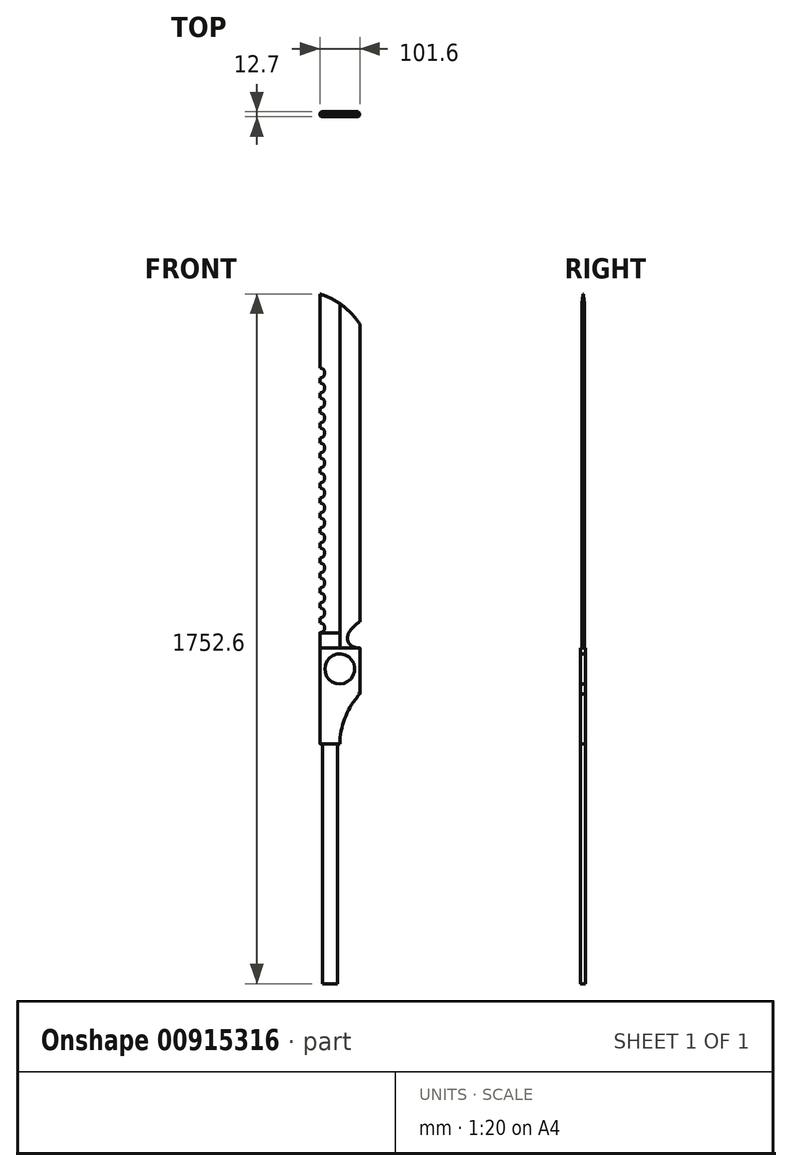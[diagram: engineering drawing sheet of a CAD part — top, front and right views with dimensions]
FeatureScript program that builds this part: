
annotation { "Feature Type Name" : "Feature", "Feature Type Description" : "" }
export const myFeature = defineFeature(function(context is Context, id is Id, definition is map)
    precondition{}
    {
        {
            var Q0;
            Q0=qCreatedBy(makeId("Front.planeOp"),FACE);
            var sketch = newSketch(context, id + "F0", { "sketchPlane" : qUnion([Q0])});
            skLineSegment(sketch, "E0", {"start": v(0, 0) * mm, "end": v(0, 381) * mm, "construction": true});
            skLineSegment(sketch, "E1", {"start": v(0, 0) * mm, "end": v(0, -609.6) * mm, "construction": true});
            skLineSegment(sketch, "E2.top", {"start": v(50.8, -762) * mm, "end": v(-50.8, -762) * mm});
            skLineSegment(sketch, "E2.left", {"start": v(50.8, 381) * mm, "end": v(50.8, -762) * mm});
            skLineSegment(sketch, "E2.right", {"start": v(-50.8, 381) * mm, "end": v(-50.8, -762) * mm});
            skPoint(sketch, "E2.middle", {"position": v(0, 0) * mm});
            skLineSegment(sketch, "E3", {"start": v(-50.8, 381) * mm, "end": v(50.8, 381) * mm});
            skLineSegment(sketch, "E4", {"start": v(25.4, 381) * mm, "end": v(25.4, 685.8) * mm, "construction": true});
            skPoint(sketch, "E5.orphan", {"position": v(0, 381) * mm});
            skPoint(sketch, "E6.orphan", {"position": v(-50.8, 762) * mm});
            skPoint(sketch, "E7.orphan", {"position": v(50.8, 762) * mm});
            skPoint(sketch, "E8.orphan", {"position": v(0, 762) * mm});
            skCircle(sketch, "E9", {"center": v(0, 190.5) * mm, "radius": 38.1 * mm});
            skPoint(sketch, "E10.orphan", {"position": v(0, 152.4) * mm});
            skLineSegment(sketch, "E11", {"start": v(0, 152.4) * mm, "end": v(0, 137.16) * mm, "construction": true});
            skLineSegment(sketch, "E12", {"start": v(-50.8, 137.16) * mm, "end": v(50.8, 137.16) * mm});
            skSolve(sketch);
        }
        {
            var Q0;
            {var subQ0=sQuery(id+"F0.wireOp",EDGE,"E3");Q0=makeQuery(id+"F0.imprint","IMPRINT",FACE,{"disambiguationData":[TD([[makeQuery(id+"F0.imprint","IMPRINT",EDGE,{"derivedFrom":subQ0}),-1.0]])]});}
            extrude(context, id + "F1", {"entities" : qUnion([Q0]), "endBound" : BoundingType.SYMMETRIC, "depth" : 12.7 * mm, "offsetDistance" : 30.48 * mm});
        }
        {
            var Q0;
            {var subQ0=sQuery(id+"F0.wireOp",EDGE,"E2.top");Q0=makeQuery(id+"F0.imprint","IMPRINT",FACE,{"disambiguationData":[TD([[makeQuery(id+"F0.imprint","IMPRINT",EDGE,{"derivedFrom":subQ0}),-1.0]])]});}
            extrude(context, id + "F2", {"entities" : qUnion([Q0]), "operationType" : NewBodyOperationType.ADD, "endBound" : BoundingType.SYMMETRIC, "depth" : 6.35 * mm, "offsetDistance" : 25.4 * mm});
        }
        {
            var Q0;
            Q0=makeQuery(id+"F1.opExtrude","SWEPT_FACE",FACE,{"disambiguationData":[OSD([sQuery(id+"F0.wireOp",EDGE,"E3")])]});
            var sketch = newSketch(context, id + "F3", { "sketchPlane" : qUnion([Q0])});
            skPoint(sketch, "E13.0", {"position": v(25.4, 0) * mm});
            skEllipse(sketch, "E14", {"center": v(25.4, 0) * mm, "majorRadius": 19.05 * mm, "minorRadius": 6.35 * mm, "majorAxis": v(-1, 0)});
            skSolve(sketch);
        }
        {
            var Q0;
            Q0 = qSketchRegion(id + "F3", true);
            extrude(context, id + "F4", {"entities" : qUnion([Q0]), "depth" : 609.6 * mm, "offsetDistance" : 30.48 * mm});
        }
        {
            var Q0;
            Q0=sQuery(id+"F0.wireOp",EDGE,"E12");
            cPlane(context, id + "F5", {"entities" : qUnion([Q0]), "cplaneType" : CPlaneType.LINE_ANGLE, "offset" : 25.4 * mm, "angle" : 90 * degree, "width" : 152.4 * mm, "height" : 152.4 * mm});
        }
        {
            var Q0;
            Q0=qCreatedBy(id+"F5.planeOp",FACE);
            var sketch = newSketch(context, id + "F6", { "sketchPlane" : qUnion([Q0])});
            skPoint(sketch, "E15.0", {"position": v(0, 0) * mm});
            skLineSegment(sketch, "E16", {"start": v(0, 0) * mm, "end": v(-50.8, 0) * mm, "construction": true});
            skPoint(sketch, "E17.0", {"position": v(-50.8, 0) * mm});
            skPoint(sketch, "E18.0", {"position": v(-50.8, 3.17) * mm});
            skPoint(sketch, "E19.0", {"position": v(-50.8, -3.17) * mm});
            skLineSegment(sketch, "E20", {"start": v(-50.8, 0) * mm, "end": v(0, 3.17) * mm});
            skLineSegment(sketch, "E21", {"start": v(0, 3.17) * mm, "end": v(-60.26, 3.17) * mm});
            skLineSegment(sketch, "E22", {"start": v(-60.26, 3.17) * mm, "end": v(-60.26, -3.17) * mm});
            skLineSegment(sketch, "E23.MirrorCS", {"start": v(-50.8, 0) * mm, "end": v(0, -3.17) * mm});
            skLineSegment(sketch, "E24.MirrorCS", {"start": v(0, -3.17) * mm, "end": v(-60.26, -3.17) * mm});
            skPoint(sketch, "E25.orphan", {"position": v(-60.26, 3.18) * mm});
            skPoint(sketch, "E26.0", {"position": v(0, -3.17) * mm});
            skPoint(sketch, "E27.0", {"position": v(0, 3.18) * mm});
            skSolve(sketch);
        }
        {
            var Q0;
            Q0 = qSketchRegion(id + "F6", true);
            extrude(context, id + "F7", {"entities" : qUnion([Q0]), "operationType" : NewBodyOperationType.REMOVE, "endBound" : BoundingType.THROUGH_ALL, "oppositeDirection" : true, "depth" : 30.48 * mm, "offsetDistance" : 30.48 * mm});
        }
        {
            var Q0;
            Q0=makeQuery(id+"F1.opExtrude","CAP_FACE",FACE,{"disambiguationData":[OSD([sQuery(id+"F0.wireOp",EDGE,"E2.top"),sQuery(id+"F0.wireOp",EDGE,"E2.left"),sQuery(id+"F0.wireOp",EDGE,"E2.right"),sQuery(id+"F0.wireOp",EDGE,"E3"),sQuery(id+"F0.wireOp",EDGE,"E9")])],"isStart":false});
            var sketch = newSketch(context, id + "F8", { "sketchPlane" : qUnion([Q0])});
            skLineSegment(sketch, "E28.direction1", {"start": v(-50.8, 365.76) * mm, "end": v(-25.8, 365.76) * mm, "construction": true});
            skCircle(sketch, "E29.0", {"center": v(0, 190.5) * mm, "radius": 38.1 * mm, "construction": true});
            skLineSegment(sketch, "E30", {"start": v(38.1, 190.5) * mm, "end": v(50.8, 190.5) * mm, "construction": true});
            skLineSegment(sketch, "E31", {"start": v(50.8, 190.5) * mm, "end": v(50.8, 99.06) * mm, "construction": true});
            skLineSegment(sketch, "E32", {"start": v(50.8, 99.06) * mm, "end": v(50.8, 73.66) * mm, "construction": true});
            skArc(sketch, "E33", {"start": v(50.8, 99.06) * mm, "mid": v(38.1, 86.36) * mm, "end": v(50.8, 73.66) * mm});
            skArc(sketch, "E34.0.1.0", {"start": v(50.8, 60.96) * mm, "mid": v(38.1, 48.26) * mm, "end": v(50.8, 35.56) * mm});
            skArc(sketch, "E34.0.2.0", {"start": v(50.8, 22.86) * mm, "mid": v(38.1, 10.16) * mm, "end": v(50.8, -2.54) * mm});
            skArc(sketch, "E34.0.3.0", {"start": v(50.8, -15.24) * mm, "mid": v(38.1, -27.94) * mm, "end": v(50.8, -40.64) * mm});
            skArc(sketch, "E34.0.4.0", {"start": v(50.8, -53.34) * mm, "mid": v(38.1, -66.04) * mm, "end": v(50.8, -78.74) * mm});
            skArc(sketch, "E34.0.5.0", {"start": v(50.8, -91.44) * mm, "mid": v(38.1, -104.14) * mm, "end": v(50.8, -116.84) * mm});
            skArc(sketch, "E34.0.6.0", {"start": v(50.8, -129.54) * mm, "mid": v(38.1, -142.24) * mm, "end": v(50.8, -154.94) * mm});
            skArc(sketch, "E34.0.7.0", {"start": v(50.8, -167.64) * mm, "mid": v(38.1, -180.34) * mm, "end": v(50.8, -193.04) * mm});
            skArc(sketch, "E34.0.8.0", {"start": v(50.8, -205.74) * mm, "mid": v(38.1, -218.44) * mm, "end": v(50.8, -231.14) * mm});
            skArc(sketch, "E34.0.9.0", {"start": v(50.8, -243.84) * mm, "mid": v(38.1, -256.54) * mm, "end": v(50.8, -269.24) * mm});
            skArc(sketch, "E34.0.10.0", {"start": v(50.8, -281.94) * mm, "mid": v(38.1, -294.64) * mm, "end": v(50.8, -307.34) * mm});
            skArc(sketch, "E34.0.11.0", {"start": v(50.8, -320.04) * mm, "mid": v(38.1, -332.74) * mm, "end": v(50.8, -345.44) * mm});
            skArc(sketch, "E34.0.12.0", {"start": v(50.8, -358.14) * mm, "mid": v(38.1, -370.84) * mm, "end": v(50.8, -383.54) * mm});
            skArc(sketch, "E34.0.13.0", {"start": v(50.8, -396.24) * mm, "mid": v(38.1, -408.94) * mm, "end": v(50.8, -421.64) * mm});
            skArc(sketch, "E34.0.14.0", {"start": v(50.8, -434.34) * mm, "mid": v(38.1, -447.04) * mm, "end": v(50.8, -459.74) * mm});
            skLineSegment(sketch, "E34.direction1", {"start": v(50.8, 73.66) * mm, "end": v(76.2, 73.66) * mm, "construction": true});
            skLineSegment(sketch, "E34.direction2", {"start": v(50.8, 73.66) * mm, "end": v(50.8, 35.56) * mm, "construction": true});
            skArc(sketch, "E35.0.0.15", {"start": v(50.8, -472.44) * mm, "mid": v(38.1, -485.14) * mm, "end": v(50.8, -497.84) * mm});
            skArc(sketch, "E35.0.0.16", {"start": v(50.8, -510.54) * mm, "mid": v(38.1, -523.24) * mm, "end": v(50.8, -535.94) * mm});
            skArc(sketch, "E35.0.0.17", {"start": v(50.8, -548.64) * mm, "mid": v(38.1, -561.34) * mm, "end": v(50.8, -574.04) * mm});
            skLineSegment(sketch, "E36", {"start": v(50.8, 99.06) * mm, "end": v(50.8, 73.66) * mm});
            skLineSegment(sketch, "E37", {"start": v(50.8, 60.96) * mm, "end": v(50.8, 35.56) * mm});
            skLineSegment(sketch, "E38", {"start": v(50.8, 22.86) * mm, "end": v(50.8, -2.54) * mm});
            skLineSegment(sketch, "E39", {"start": v(50.8, -15.24) * mm, "end": v(50.8, -40.64) * mm});
            skLineSegment(sketch, "E40", {"start": v(50.8, -53.34) * mm, "end": v(50.8, -78.74) * mm});
            skLineSegment(sketch, "E41", {"start": v(50.8, -91.44) * mm, "end": v(50.8, -116.84) * mm});
            skLineSegment(sketch, "E42", {"start": v(50.8, -129.54) * mm, "end": v(50.8, -154.94) * mm});
            skLineSegment(sketch, "E43", {"start": v(50.8, -167.64) * mm, "end": v(50.8, -193.04) * mm});
            skLineSegment(sketch, "E44", {"start": v(50.8, -205.74) * mm, "end": v(50.8, -231.14) * mm});
            skLineSegment(sketch, "E45", {"start": v(50.8, -243.84) * mm, "end": v(50.8, -269.24) * mm});
            skLineSegment(sketch, "E46", {"start": v(50.8, -281.94) * mm, "end": v(50.8, -307.34) * mm});
            skLineSegment(sketch, "E47", {"start": v(50.8, -320.04) * mm, "end": v(50.8, -345.44) * mm});
            skLineSegment(sketch, "E48", {"start": v(50.8, -358.14) * mm, "end": v(50.8, -383.54) * mm});
            skLineSegment(sketch, "E49", {"start": v(50.8, -396.24) * mm, "end": v(50.8, -421.64) * mm});
            skLineSegment(sketch, "E50", {"start": v(50.8, -434.34) * mm, "end": v(50.8, -459.74) * mm});
            skLineSegment(sketch, "E51", {"start": v(50.8, -472.44) * mm, "end": v(50.8, -497.84) * mm});
            skLineSegment(sketch, "E52", {"start": v(50.8, -510.54) * mm, "end": v(50.8, -535.94) * mm});
            skLineSegment(sketch, "E53", {"start": v(50.8, -548.64) * mm, "end": v(50.8, -574.04) * mm});
            skArc(sketch, "E54.0.0.18", {"start": v(50.8, -586.74) * mm, "mid": v(38.1, -599.44) * mm, "end": v(50.8, -612.14) * mm});
            skArc(sketch, "E54.0.0.19", {"start": v(50.8, -624.84) * mm, "mid": v(38.1, -637.54) * mm, "end": v(50.8, -650.24) * mm});
            skArc(sketch, "E55.0.0.20", {"start": v(50.8, -662.94) * mm, "mid": v(38.1, -675.64) * mm, "end": v(50.8, -688.34) * mm});
            skArc(sketch, "E55.0.0.21", {"start": v(50.8, -701.04) * mm, "mid": v(38.1, -713.74) * mm, "end": v(50.8, -726.44) * mm});
            skLineSegment(sketch, "E56", {"start": v(-50.8, 381) * mm, "end": v(0, 381) * mm});
            skLineSegment(sketch, "E57", {"start": v(-50.8, 381) * mm, "end": v(-50.8, 254) * mm});
            skArc(sketch, "E58", {"start": v(-50.8, 254) * mm, "mid": v(-14.01, 312.95) * mm, "end": v(0, 381) * mm});
            skSolve(sketch);
        }
        {
            var Q0;
            Q0 = qSketchRegion(id + "F8", true);
            extrude(context, id + "F9", {"entities" : qUnion([Q0]), "operationType" : NewBodyOperationType.REMOVE, "oppositeDirection" : true, "depth" : 30.48 * mm, "offsetDistance" : 30.48 * mm});
        }
        {
            var Q0;
            Q0=makeQuery(id+"F1.opExtrude","CAP_EDGE",EDGE,{"disambiguationData":[OSD([sQuery(id+"F0.wireOp",EDGE,"E9")])],"isStart":false});
            var Q1;
            Q1=makeQuery(id+"F1.opExtrude","CAP_EDGE",EDGE,{"disambiguationData":[OSD([sQuery(id+"F0.wireOp",EDGE,"E9")])],"isStart":true});
            fillet(context, id + "F10", {"entities" : qUnion([Q0, Q1]), "tangentPropagation" : true, "radius" : 6.35 * mm, "defaultsChanged" : true, "vertexSettings" : [], "allowEdgeOverflow" : false});
        }
        {
            var Q0;
            Q0=makeQuery(id+"F1.opExtrude","SWEPT_BODY",BODY,{"disambiguationData":[OSD([sQuery(id+"F0.wireOp",EDGE,"E2.top"),sQuery(id+"F0.wireOp",EDGE,"E2.left"),sQuery(id+"F0.wireOp",EDGE,"E2.right"),sQuery(id+"F0.wireOp",EDGE,"E3"),sQuery(id+"F0.wireOp",EDGE,"E9")])]});
            var Q1;
            Q1=makeQuery(id+"F4.opExtrude","SWEPT_BODY",BODY,{"disambiguationData":[OSD([sQuery(id+"F3.wireOp",EDGE,"E14")])]});
            var Q2;
            {var subQ0=sQuery(id+"F0.wireOp",EDGE,"E9");Q2=makeQuery(id+"F10.opFillet","BLEND_EDGE",EDGE,{"blendedFrom":[makeQuery(id+"F1.opExtrude","CAP_EDGE",EDGE,{"disambiguationData":[OSD([subQ0])],"isStart":false}),makeQuery(id+"F1.opExtrude","CAP_FACE",FACE,{"disambiguationData":[OSD([sQuery(id+"F0.wireOp",EDGE,"E2.top"),sQuery(id+"F0.wireOp",EDGE,"E2.left"),sQuery(id+"F0.wireOp",EDGE,"E2.right"),sQuery(id+"F0.wireOp",EDGE,"E3"),subQ0])],"isStart":false})],"blendedInto":[makeQuery(id+"F1.opExtrude","CAP_FACE",FACE,{"disambiguationData":[OSD([sQuery(id+"F0.wireOp",EDGE,"E2.top"),sQuery(id+"F0.wireOp",EDGE,"E2.left"),sQuery(id+"F0.wireOp",EDGE,"E2.right"),sQuery(id+"F0.wireOp",EDGE,"E3"),subQ0])],"isStart":false})]});}
            transform(context, id + "F11", {"entities" : qUnion([Q0, Q1]), "transformType" : TransformType.ROTATION, "transformAxis" : qUnion([Q2]), "angle" : 180 * degree, "makeCopy" : false});
        }
        {
            var Q0;
            Q0=qCreatedBy(makeId("Top.planeOp"),FACE);
            var Q1;
            Q1=makeQuery(id+"F9.boolean.opBoolean","INTERSECT",VERTEX,{"disambiguationData":[OD(1.0)],"derivedFrom":[makeQuery(id+"F2.opExtrude","CAP_FACE",FACE,{"disambiguationData":[OSD([sQuery(id+"F0.wireOp",EDGE,"E2.top"),sQuery(id+"F0.wireOp",EDGE,"E2.left"),sQuery(id+"F0.wireOp",EDGE,"E2.right"),sQuery(id+"F0.wireOp",EDGE,"E12")])],"isStart":false}),makeQuery(id+"F9.opExtrude","SWEPT_FACE",FACE,{"disambiguationData":[OSD([sQuery(id+"F8.wireOp",EDGE,"E35.0.0.17")])]})]});
            cPlane(context, id + "F12", {"entities" : qUnion([Q0, Q1]), "cplaneType" : CPlaneType.PLANE_POINT, "offset" : 25.4 * mm, "width" : 152.4 * mm, "height" : 152.4 * mm});
        }
        {
            var Q0;
            Q0=qCreatedBy(id+"F12.planeOp",FACE);
            cPlane(context, id + "F13", {"entities" : qUnion([Q0]), "cplaneType" : CPlaneType.OFFSET, "offset" : 12.7 * mm, "width" : 152.4 * mm, "height" : 152.4 * mm});
        }
        {
            var Q0;
            Q0=qCreatedBy(id+"F13.planeOp",FACE);
            var sketch = newSketch(context, id + "F14", { "sketchPlane" : qUnion([Q0])});
            skPoint(sketch, "E59.0", {"position": v(-50.8, 0) * mm});
            skPoint(sketch, "E60.0", {"position": v(0, 3.18) * mm});
            skLineSegment(sketch, "E61", {"start": v(-59.4, 0) * mm, "end": v(-59.4, -1.9) * mm});
            skPoint(sketch, "E62.0", {"position": v(0, -3.18) * mm});
            skLineSegment(sketch, "E63", {"start": v(-50.8, 0) * mm, "end": v(0, 3.18) * mm});
            skLineSegment(sketch, "E64", {"start": v(0, 3.18) * mm, "end": v(-59.4, 3.17) * mm});
            skLineSegment(sketch, "E65", {"start": v(-59.4, 3.17) * mm, "end": v(-59.4, -1.9) * mm});
            skLineSegment(sketch, "E66", {"start": v(-50.8, 0) * mm, "end": v(-59.4, 0) * mm, "construction": true});
            skLineSegment(sketch, "E67.MirrorCS", {"start": v(-50.8, 0) * mm, "end": v(0, -3.18) * mm});
            skLineSegment(sketch, "E68.MirrorCS", {"start": v(0, -3.17) * mm, "end": v(-59.4, -3.17) * mm});
            skLineSegment(sketch, "E69.MirrorCS", {"start": v(-59.4, -3.17) * mm, "end": v(-59.4, 1.9) * mm});
            skSolve(sketch);
        }
        {
            var Q0;
            Q0=makeQuery(id+"F1.opExtrude","CAP_EDGE",EDGE,{"disambiguationData":[OSD([sQuery(id+"F0.wireOp",EDGE,"E2.left")])],"isStart":false});
            var Q1;
            Q1=makeQuery(id+"F1.opExtrude","CAP_EDGE",EDGE,{"disambiguationData":[OSD([sQuery(id+"F0.wireOp",EDGE,"E2.left")])],"isStart":true});
            fillet(context, id + "F15", {"entities" : qUnion([Q0, Q1]), "radius" : 6.35 * mm, "defaultsChanged" : false, "vertexSettings" : [], "allowEdgeOverflow" : false});
        }
        {
            var Q0;
            Q0=makeQuery(id+"F9.boolean.opBoolean","COPY",EDGE,{"derivedFrom":makeQuery(id+"F9.opExtrude","CAP_EDGE",EDGE,{"disambiguationData":[OSD([sQuery(id+"F8.wireOp",EDGE,"E58")])],"isStart":true})});
            var Q1;
            Q1=makeQuery(id+"F1.opExtrude","CAP_EDGE",EDGE,{"disambiguationData":[OSD([sQuery(id+"F0.wireOp",EDGE,"E2.right")])],"isStart":false});
            var Q2;
            Q2=makeQuery(id+"F1.opExtrude","CAP_EDGE",EDGE,{"disambiguationData":[OSD([sQuery(id+"F0.wireOp",EDGE,"E2.right")])],"isStart":true});
            var Q3;
            Q3=makeQuery(id+"F9.boolean.opBoolean","INTERSECT",EDGE,{"derivedFrom":[makeQuery(id+"F1.opExtrude","CAP_FACE",FACE,{"disambiguationData":[OSD([sQuery(id+"F0.wireOp",EDGE,"E2.left"),sQuery(id+"F0.wireOp",EDGE,"E2.right"),sQuery(id+"F0.wireOp",EDGE,"E3"),sQuery(id+"F0.wireOp",EDGE,"E9"),sQuery(id+"F0.wireOp",EDGE,"E12")])],"isStart":true}),makeQuery(id+"F9.opExtrude","SWEPT_FACE",FACE,{"disambiguationData":[OSD([sQuery(id+"F8.wireOp",EDGE,"E58")])]})]});
            fillet(context, id + "F16", {"entities" : qUnion([Q0, Q1, Q2, Q3]), "tangentPropagation" : true, "radius" : 6.35 * mm, "defaultsChanged" : true, "vertexSettings" : [], "allowEdgeOverflow" : false});
        }
        {
            var Q0;
            Q0=qCreatedBy(makeId("Front.planeOp"),FACE);
            var sketch = newSketch(context, id + "F17", { "sketchPlane" : qUnion([Q0])});
            skLineSegment(sketch, "E70.0", {"start": v(-44.45, -609.6) * mm, "end": v(-6.35, -609.6) * mm, "construction": true});
            skLineSegment(sketch, "E71", {"start": v(-6.35, -609.6) * mm, "end": v(92.79, -609.6) * mm, "construction": true});
            skLineSegment(sketch, "E72", {"start": v(0, 0) * mm, "end": v(0, 381) * mm, "construction": true});
            skPoint(sketch, "E73.0", {"position": v(0, 1143) * mm});
            skPoint(sketch, "E74.0", {"position": v(-50.8, 1143) * mm});
            skPoint(sketch, "E75.0", {"position": v(50.8, 1143) * mm});
            skLineSegment(sketch, "E76", {"start": v(50.8, 1066.8) * mm, "end": v(50.8, 1143) * mm});
            skLineSegment(sketch, "E77", {"start": v(-50.8, 1143) * mm, "end": v(50.8, 1143) * mm});
            skArc(sketch, "E78", {"start": v(50.8, 1066.8) * mm, "mid": v(6.53, 1113.6) * mm, "end": v(-50.8, 1143) * mm});
            skSolve(sketch);
        }
        {
            var Q0;
            Q0 = qSketchRegion(id + "F17", true);
            extrude(context, id + "F18", {"entities" : qUnion([Q0]), "operationType" : NewBodyOperationType.REMOVE, "endBound" : BoundingType.SYMMETRIC, "oppositeDirection" : true, "depth" : 25.4 * mm, "offsetDistance" : 25.4 * mm});
        }
        {
            var Q0;
            Q0 = qSketchRegion(id + "F14", true);
            var Q1;
            {var subQ0=sQuery(id+"F0.wireOp",EDGE,"E2.left");Q1=makeQuery(id+"F15.opFillet","BLEND_VERTEX",VERTEX,{"blendedFrom":[makeQuery(id+"F1.opExtrude","CAP_EDGE",EDGE,{"disambiguationData":[OSD([subQ0])],"isStart":false}),makeQuery(id+"F9.boolean.opBoolean","COPY",FACE,{"derivedFrom":makeQuery(id+"F9.opExtrude","SWEPT_FACE",FACE,{"disambiguationData":[OSD([sQuery(id+"F8.wireOp",EDGE,"E33")])]})}),makeQuery(id+"F2.opExtrude","CAP_FACE",FACE,{"disambiguationData":[OSD([sQuery(id+"F0.wireOp",EDGE,"E2.top"),subQ0,sQuery(id+"F0.wireOp",EDGE,"E2.right"),sQuery(id+"F0.wireOp",EDGE,"E12")])],"isStart":false})],"blendedInto":[makeQuery(id+"F9.boolean.opBoolean","COPY",FACE,{"derivedFrom":makeQuery(id+"F9.opExtrude","SWEPT_FACE",FACE,{"disambiguationData":[OSD([sQuery(id+"F8.wireOp",EDGE,"E33")])]})}),makeQuery(id+"F2.opExtrude","CAP_FACE",FACE,{"disambiguationData":[OSD([sQuery(id+"F0.wireOp",EDGE,"E2.top"),subQ0,sQuery(id+"F0.wireOp",EDGE,"E2.right"),sQuery(id+"F0.wireOp",EDGE,"E12")])],"isStart":false})]});}
            extrude(context, id + "F19", {"entities" : qUnion([Q0]), "operationType" : NewBodyOperationType.REMOVE, "endBound" : BoundingType.UP_TO_VERTEX, "oppositeDirection" : true, "depth" : 25.4 * mm, "endBoundEntityVertex" : qUnion([Q1]), "offsetDistance" : 25.4 * mm, "hasSecondDirection" : true, "secondDirectionBound" : SecondDirectionBoundingType.THROUGH_ALL, "secondDirectionOppositeDirection" : false, "secondDirectionDepth" : 25.4 * mm});
        }
        {
            var Q0;
            Q0=qCreatedBy(makeId("Front.planeOp"),FACE);
            var sketch = newSketch(context, id + "F20", { "sketchPlane" : qUnion([Q0])});
            skPoint(sketch, "E79.0", {"position": v(0, 243.84) * mm});
            skPoint(sketch, "E80.0", {"position": v(0, 281.97) * mm});
            skLineSegment(sketch, "E81.0", {"start": v(50.8, 1066.8) * mm, "end": v(50.8, 309.9) * mm, "construction": true});
            skPoint(sketch, "E82", {"position": v(50.8, 281.97) * mm});
            skPoint(sketch, "E83", {"position": v(50.8, 309.9) * mm});
            skLineSegment(sketch, "E84.trimOffspring", {"start": v(50.8, 281.97) * mm, "end": v(50.8, 243.84) * mm, "construction": true});
            skLineSegment(sketch, "E85", {"start": v(0, 243.84) * mm, "end": v(0, 188.75) * mm, "construction": true});
            skLineSegment(sketch, "E86", {"start": v(12.7, 243.84) * mm, "end": v(50.8, 243.84) * mm});
            skLineSegment(sketch, "E87", {"start": v(50.8, 243.84) * mm, "end": v(50.8, 309.9) * mm});
            skLineSegment(sketch, "E88.0", {"start": v(12.7, 243.84) * mm, "end": v(12.7, 188.75) * mm});
            skArc(sketch, "E89", {"start": v(50.8, 309.9) * mm, "mid": v(22.9, 281.97) * mm, "end": v(12.7, 243.84) * mm});
            skSolve(sketch);
        }
        {
            var Q0;
            Q0 = qSketchRegion(id + "F20", true);
            extrude(context, id + "F21", {"entities" : qUnion([Q0]), "operationType" : NewBodyOperationType.REMOVE, "endBound" : BoundingType.SYMMETRIC, "depth" : 25.4 * mm, "offsetDistance" : 25.4 * mm});
        }
        {
            var Q0;
            Q0=makeQuery(id+"F21.boolean.opBoolean","COPY",EDGE,{"derivedFrom":makeQuery(id+"F21.opExtrude","SWEPT_EDGE",EDGE,{"disambiguationData":[OSD([sQuery(id+"F20.wireOp",EDGE,"E86"),sQuery(id+"F20.wireOp",EDGE,"E89")])]})});
            fillet(context, id + "F22", {"entities" : qUnion([Q0]), "tangentPropagation" : true, "radius" : 25.4 * mm, "defaultsChanged" : true, "vertexSettings" : [], "allowEdgeOverflow" : false});
        }
    });
